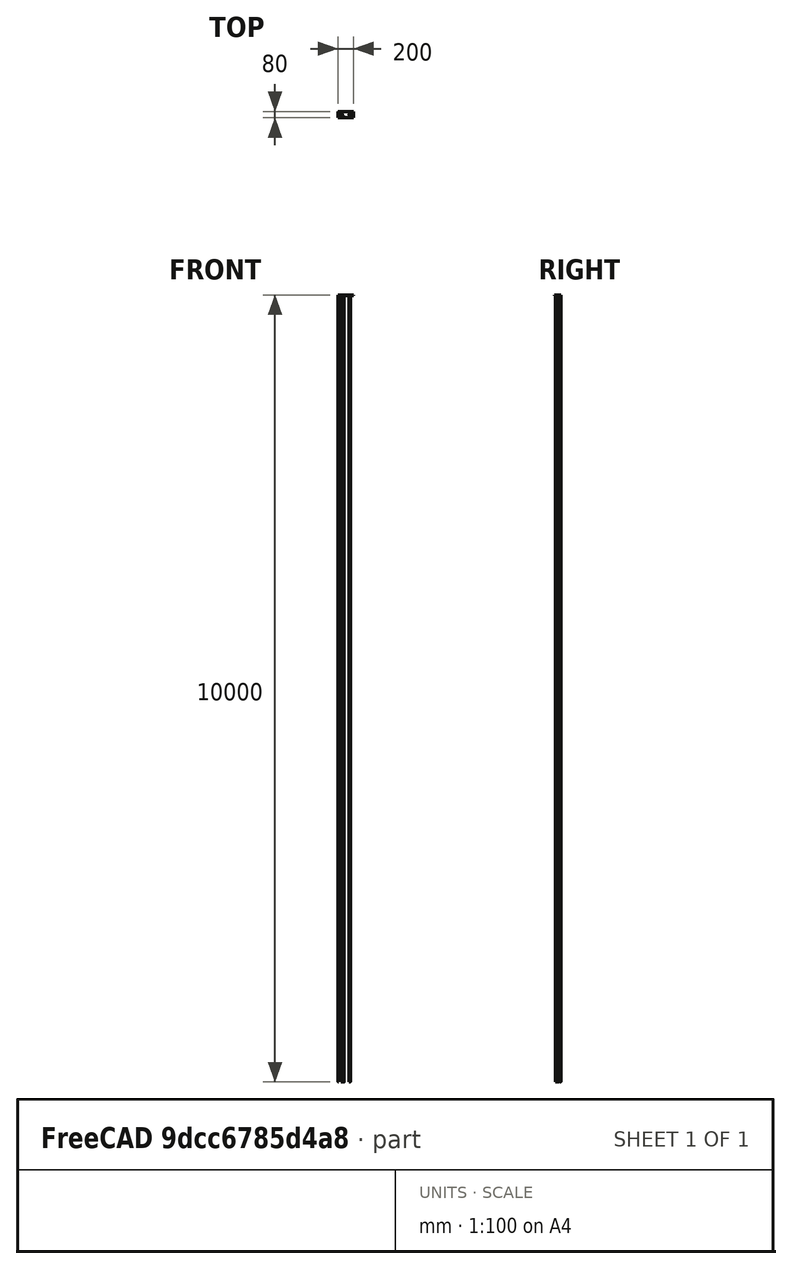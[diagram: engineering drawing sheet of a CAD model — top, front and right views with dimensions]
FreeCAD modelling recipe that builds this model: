
FCSTD DOCUMENT  (FreeCAD 0.14R3700 (Git))
Label: slide_rail_mount_right
License: CC-BY 3.0
LicenseURL: http://creativecommons.org/licenses/by/3.0/
objects: Mesh::Feature×8, Sketcher::SketchObject×2, PartDesign::Pocket×2, Part::Box×1
note: 7 computed .brp shape members not serialized (recipe doc carries the construction recipe); baked Part::Feature solids carry a one-line shape summary decoded from their .brp

FEATURE [Part::Box] Box  label="Cube"
  Height = 6
  Length = 200
  Width = 80
FEATURE [Sketcher::SketchObject] Sketch
  Placement = pos=(0,0,6) rot=(0,0,1;0rad)
  Support = -> Box [Face6]
  sketch-geometry (4):
    g0: Circle CenterX=50 CenterY=40 CenterZ=0 NormalX=0 NormalY=0 NormalZ=1 Radius=10.1
    g1: Circle CenterX=75 CenterY=15 CenterZ=0 NormalX=0 NormalY=0 NormalZ=1 Radius=6
    g2: Circle CenterX=150 CenterY=40 CenterZ=0 NormalX=0 NormalY=0 NormalZ=1 Radius=10.1
    g3: Circle CenterX=4.93925 CenterY=75.1029 CenterZ=0 NormalX=0 NormalY=0 NormalZ=1 Radius=2.5
  constraints (10):
    c: Radius(g0) = 10.1
    c: Radius(g1) = 6
    c: Equal(g0,g2)
    c: DistanceY(g-1,g2) = 40
    c: DistanceX(g-1,g0) = 50
    c: DistanceX(g1) = 75
    c: DistanceY(g-1,g1) = 15
    c: DistanceX(g2,g0) = -100
    c: DistanceY(g-1,g0) = 40
    c: Radius(g3) = 2.5
FEATURE [PartDesign::Pocket] Pocket
  Length = 5
  Sketch = -> Sketch
  Type = 1
FEATURE [Mesh::Feature] lm8uu_round_split_xnaron  label="lm8uu-round-split-xnaron"
  Placement = pos=(0,1,30) rot=(-1,0,0;1.5708rad)
FEATURE [Mesh::Feature] lm8uu_round_split_xnaron001  label="lm8uu-round-split-xnaron001"
  Placement = pos=(0,55,30) rot=(-1,0,0;1.5708rad)
FEATURE [Mesh::Feature] lm8uu_round_split_xnaron002  label="lm8uu-round-split-xnaron002"
  Placement = pos=(158,55,30) rot=(-1,0,0;1.5708rad)
FEATURE [Mesh::Feature] lm8uu_round_split_xnaron003  label="lm8uu-round-split-xnaron003"
  Placement = pos=(158,1,30) rot=(-1,0,0;1.5708rad)
FEATURE [Mesh::Feature] lm8uu_bearing
  Placement = pos=(20,1,18) rot=(0.57735,-0.57735,-0.57735;4.18879rad)
FEATURE [Mesh::Feature] lm8uu_bearing001
  Placement = pos=(20,55,18) rot=(0.57735,-0.57735,-0.57735;4.18879rad)
FEATURE [Mesh::Feature] lm8uu_bearing002
  Placement = pos=(179,55,18) rot=(0.57735,-0.57735,-0.57735;4.18879rad)
FEATURE [Mesh::Feature] lm8uu_bearing003
  Placement = pos=(179,1,18) rot=(0.57735,-0.57735,-0.57735;4.18879rad)
FEATURE [Sketcher::SketchObject] Sketch001
  Placement = pos=(0,0,6) rot=(0,0,1;0rad)
  Support = -> Box [Face6]
  sketch-geometry (4):
    g0: Circle CenterX=50 CenterY=40 CenterZ=0 NormalX=0 NormalY=0 NormalZ=1 Radius=10.1
    g1: Circle CenterX=75 CenterY=15 CenterZ=0 NormalX=0 NormalY=0 NormalZ=1 Radius=6
    g2: Circle CenterX=150 CenterY=40 CenterZ=0 NormalX=0 NormalY=0 NormalZ=1 Radius=10.1
    g3: Circle CenterX=4.93925 CenterY=75.1029 CenterZ=0 NormalX=0 NormalY=0 NormalZ=1 Radius=2.5
  constraints (10):
    c: Radius(g0) = 10.1
    c: Radius(g1) = 6
    c: Equal(g0,g2)
    c: DistanceY(g-1,g2) = 40
    c: DistanceX(g-1,g0) = 50
    c: DistanceX(g1) = 75
    c: DistanceY(g-1,g1) = 15
    c: DistanceX(g2,g0) = -100
    c: DistanceY(g-1,g0) = 40
    c: Radius(g3) = 2.5
FEATURE [PartDesign::Pocket] Pocket001
  Length = 5
  Sketch = -> Sketch001
  Type = 1
